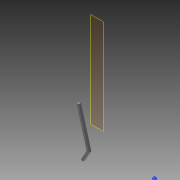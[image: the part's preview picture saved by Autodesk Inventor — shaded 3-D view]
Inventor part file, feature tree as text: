
AUTODESK INVENTOR PART (.ipt)
format: ipt  version: 2013 (Build 170138000, 138)  size: 117,248 bytes
history: native  units: in
note: dims shown in document units (in); Inventor stores cm internally (conversion verified against a paired STEP export)
features: extrude x2, sketch x2, plane x1
ambient origin geometry x8: Origin, YZ Plane, XZ Plane, XY Plane, X Axis, Y Axis, Z Axis, Center Point
bodies: Solid1 (feature_tree)
feature tree (5):
  plane  "Work Plane1"
  extrude  "Extrusion1"  Depth=19.0in
  extrude  "Extrusion2"  TaperAngle=0.0deg  [1 undecoded]
  sketch  "Sketch1"  dims[d0=2.5in d1=19.0in]
  sketch  "Sketch2"  dims[d2=7.0in d3=0.0in d4=5.0in d5=3.0in d6=17.0in d7=90.0deg d8=0.5in d9=90.0deg d10=10.0in d11=180.0deg d12=10.0in d13=20.5in d14=4.5in d15=45.0deg d16=16.263in d17=23.505in d18=90.0deg d19=9.0in d20=0.4172in d21=1.0in d22=1.0356in d23=1.0in d25=0.7264in d26=0.5in d27=0.7264in d28=1.0in d29=0.0in d30=0.5in d31=0.25in d32=1.0in d33=0.0in]
note: 1 required parameter value undecoded (feature->parameter linkage not recoverable at this tier; creation-order binding heuristic only, values carry confidence <= 0.55)
